# Revit family: HUNTER_I-25-06
name_source: partatom
category: Sprinklers
revit_build: Autodesk Revit 2017 (Build: 20160225_1515(x64)
units: mm (PartAtom-declared; Revit-internal decimal feet)

## family parameters
Always vertical = Yes
Cut with Voids When Loaded = No
Maintain Annotation Orientation = No
OmniClass Number = 23.11.27.15.11.11
OmniClass Title = Installed Sprinkler Heads
Part Type = Normal
Room Calculation Point = No
Round Connector Dimension = Use Diameter
Shared = Yes
Work Plane-Based = No

## types (10) — shared parameters
Arc Max = 360.00°
Arc Min = 50.00°
Assembly Code = G2050700
Body Height = 260 mm  [stored 0.853018 ft]
Body Material = Hunter® ABS Plastic
Connection_Dia = 30 mm  [stored 0.0984252 ft]
Diameter = 610 mm
Exposed Diameter = 50 mm  [stored 0.164042 ft]
Inlet Size = 1" BSP
Keynote = 328423.02
Manufacturer = Hunter® Industries
Pop Up Height = 150 mm
Pop Up Material = Hunter® ABS Plastic
Riser Material = I-25-06
Show 2D Symbol = Yes
Show Water Spray = Yes
Trajectory Angle = 25.00°
Type Comments = Rotor I-25-06 with Plastic Riser
Type Image = <None>
URL = https://www.hunterindustries.com
Water = Water
Water Pattern = Water Arc

## per-type parameters (varying)
| type | Description | Model | Nozzle Size | Nozzle Tag | Precipitation Rate | Pressure | Trajectory Radius |
| I-25-06-Standard 7 Orange-5.0bar-14.90m | Hunter I-25-06 Rotor Body with Preinstalled Check in Valve and (7 Orange) Standard Nozzle | I-25-06- Standard 7 Orange | Hunter® (7 Orange) Standard Nozzle | I-25-06-7 Orange | 16 mm/hr | 500.0 kPa | 14900 mm  [stored 48.8845 ft] |
| I-25-06-Standard 10 Lt.Green-5.0bar-16.20m | Hunter I-25-06 Rotor Body with Preinstalled Check in Valve and (10 Lt. Green) Standard Nozzle | I-25-06-Standard 10 Lt. Green | Hunter® (10 Lt. Green) Standard Nozzle | I-25-06-10 Lt. Green | 21 mm/hr | 500.0 kPa | 16200 mm  [stored 53.1496 ft] |
| I-25-06-Standard 15 Grey-5.0bar-17.40m | Hunter I-25-06 Rotor Body with Preinstalled Check in Valve and (15 Grey) Standard Nozzle | I-25-06-Standard 15 Grey | Hunter® (15 Grey) Standard Nozzle | I-25-06-15 Grey | 23 mm/hr | 500.0 kPa | 17400 mm |
| I-25-06-Standard 20 Dk. Brown-5.50bar-19.50m | Hunter I-25-06 Rotor Body with Preinstalled Check in Valve and (20 Dk. Brown) Standard Nozzle | I-25-06-Standard 20 Dk. Brown | Hunter® (20 Dk. Brown) Standard Nozzle | I-25-06-20 Dk. Brown | 25 mm/hr | 550.0 kPa | 19500 mm  [stored 63.9764 ft] |
| I-25-06-Standard 25 Dk. Blue-6.0bar-21.00m | Hunter I-25-06 Rotor Body with Preinstalled Check in Valve and (25 Dk. Blue) Standard Nozzle | I-25-06- Standard 25 Dk. Blue | Hunter® (25 Dk. Blue) Standard Nozzle | I-25-06- 25 Dk. Blue | 30 mm/hr | 600.0 kPa | 21000 mm  [stored 68.8976 ft] |
| I-25-06-High speed 7 Orange-5.0bar-13.40m | Hunter I-25-06 Rotor Body with Preinstalled Check in Valve and (7 Orange) High Speed Nozzle | I-25-06-High Speed 7 Orange | Hunter® (7 Orange) High Speed Nozzle | I-25-06-High Speed 7 Orange | 21 mm/hr | 500.0 kPa | 13400 mm  [stored 43.9633 ft] |
| I-25-06-High speed 10 Lt.Green-5.0bar-14.90m | Hunter I-25-06 Rotor Body with Preinstalled Check in Valve and (10 Lt. Green) Standard Nozzle | I-25-06-High Speed 10 Lt. Green | Hunter® (10 Lt. Green) High Speed Nozzle | I-25-06-High Speed 10 Lt. Green | 25 mm/hr | 500.0 kPa | 14900 mm  [stored 48.8845 ft] |
| I-25-06-High speed 15 Grey-5.0bar-16.20m | Hunter I-25-06 Rotor Body with Preinstalled Check in Valve and (15 Grey) High Speed Nozzle | I-25-06-High Speed 15 Grey | Hunter® (15 Grey) High Speed Nozzle | I-25-06-High Speed 15 Grey | 27 mm/hr | 500.0 kPa | 16200 mm  [stored 53.1496 ft] |
| I-25-06-High speed 20 Dk. Brown-5.50bar-17.70m | Hunter I-25-06 Rotor Body with Preinstalled Check in Valve and (20 Dk. Brown) High Speed Nozzle | I-25-06-High Speed 20 Dk. Brown | Hunter® (20 Dk. Brown) High Speed Nozzle | I-25-06-High Speed 20 Dk. Brown | 30 mm/hr | 550.0 kPa | 17700 mm  [stored 58.0709 ft] |
| I-25-06-High speed 25 Dk. Blue-6.0bar-19.80m | Hunter I-25-06 Rotor Body with Preinstalled Check in Valve and (25 Dk. Blue) High Speed Nozzle | I-25-06-High Speed 25 Dk. Blue | Hunter® (25 Dk. Blue) High Speed Nozzle | I-25-06-High Speed 25 Dk. Blue | 34 mm/hr | 600.0 kPa | 19800 mm  [stored 64.9606 ft] |

note: [stored X ft] marks values corroborated as IEEE doubles in the binary element streams (Revit-internal decimal feet)

## geometry (parser evidence)
native form markers: Sweep x14
no freeform markers — native parametric forms only
